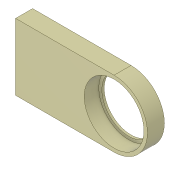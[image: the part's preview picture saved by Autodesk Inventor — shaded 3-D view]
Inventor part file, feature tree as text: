
AUTODESK INVENTOR PART (.ipt)
format: ipt  version: 2019.4 (Build 234330000, 330)  size: 114,688 bytes
history: native  units: mm
features: extrude x2, sketch x2, reference x2, other x2, plane x1, projected_geometry x1
ambient origin geometry x8: Origin, YZ Plane, XZ Plane, XY Plane, X Axis, Y Axis, Z Axis, Center Point
bodies: Solid1 (feature_tree)
feature tree (10):
  plane  "Work Plane1"
  extrude  "Extrusion1"  Depth=25.55mm
  extrude  "Extrusion2"  Depth=1.0mm TaperAngle=0.0deg
  sketch  "Sketch1"  dims[d0=0.75mm d1=25.55mm]
  reference  "Reference1"
  reference  "Reference2"
  sketch  "Sketch2"  dims[d2=23.0mm d3=1.0mm d4=0.0mm d5=25.55mm d6=6.25mm d7=0.0mm]
  projected_geometry  "Projected Loop1"
  other  "Assembly_Axiotech_Eypiece.iam"
  other  "00_Fluegeladapter:1"
